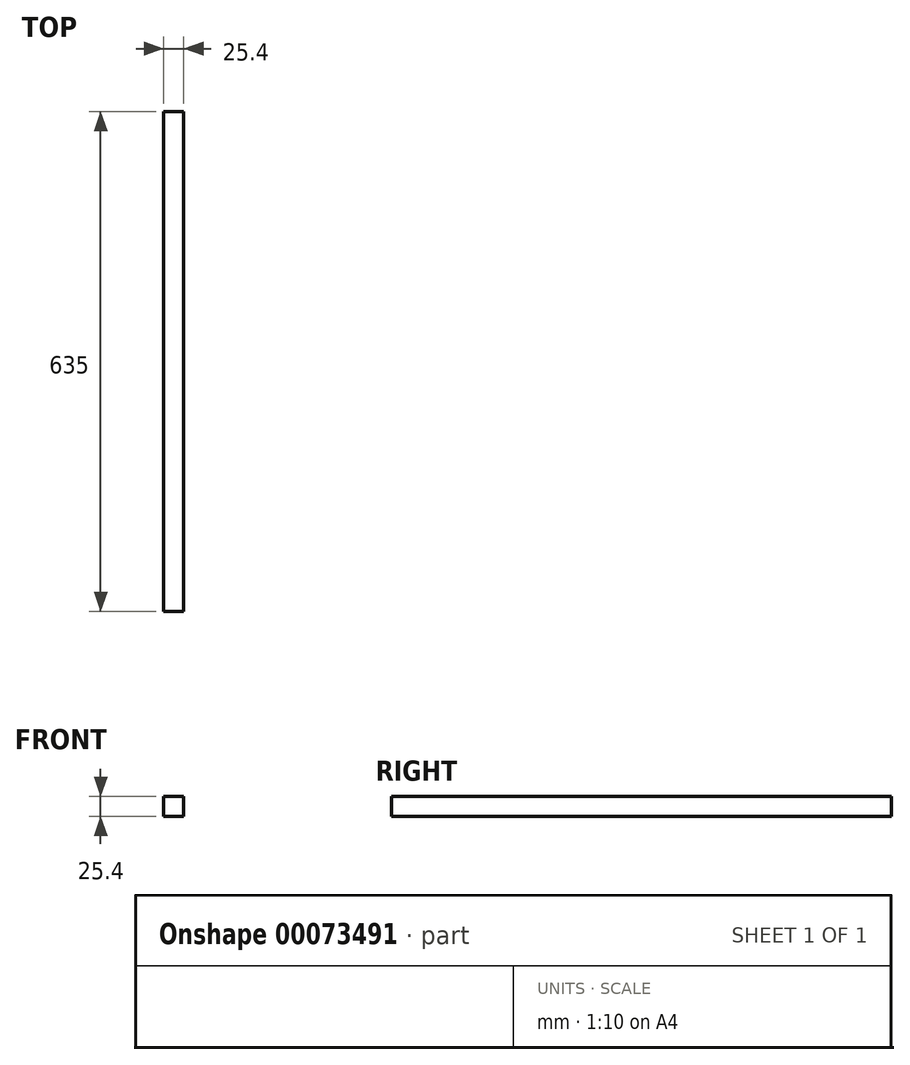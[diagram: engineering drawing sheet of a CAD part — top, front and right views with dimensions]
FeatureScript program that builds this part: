
annotation { "Feature Type Name" : "Feature", "Feature Type Description" : "" }
export const myFeature = defineFeature(function(context is Context, id is Id, definition is map)
    precondition{}
    {
        {
            var Q0;
            Q0=qCreatedBy(makeId("Front.planeOp"),FACE);
            var sketch = newSketch(context, id + "F0", { "sketchPlane" : qUnion([Q0])});
            skLineSegment(sketch, "E0.bottom", {"start": v(-7.08, -12.77) * mm, "end": v(18.32, -12.77) * mm});
            skLineSegment(sketch, "E0.top", {"start": v(-7.08, 12.63) * mm, "end": v(18.32, 12.63) * mm});
            skLineSegment(sketch, "E0.left", {"start": v(-7.08, -12.77) * mm, "end": v(-7.08, 12.63) * mm});
            skLineSegment(sketch, "E0.right", {"start": v(18.32, -12.77) * mm, "end": v(18.32, 12.63) * mm});
            skSolve(sketch);
        }
        {
            var Q0;
            Q0=makeQuery(id+"F0.imprint","IMPRINT",FACE,{"disambiguationData":[TD([[makeQuery(id+"F0.imprint","IMPRINT",EDGE,{"derivedFrom":sQuery(id+"F0.wireOp",EDGE,"E0.bottom")}),1.0]])]});
            extrude(context, id + "F1", {"entities" : qUnion([Q0]), "depth" : 635 * mm});
        }
    });
